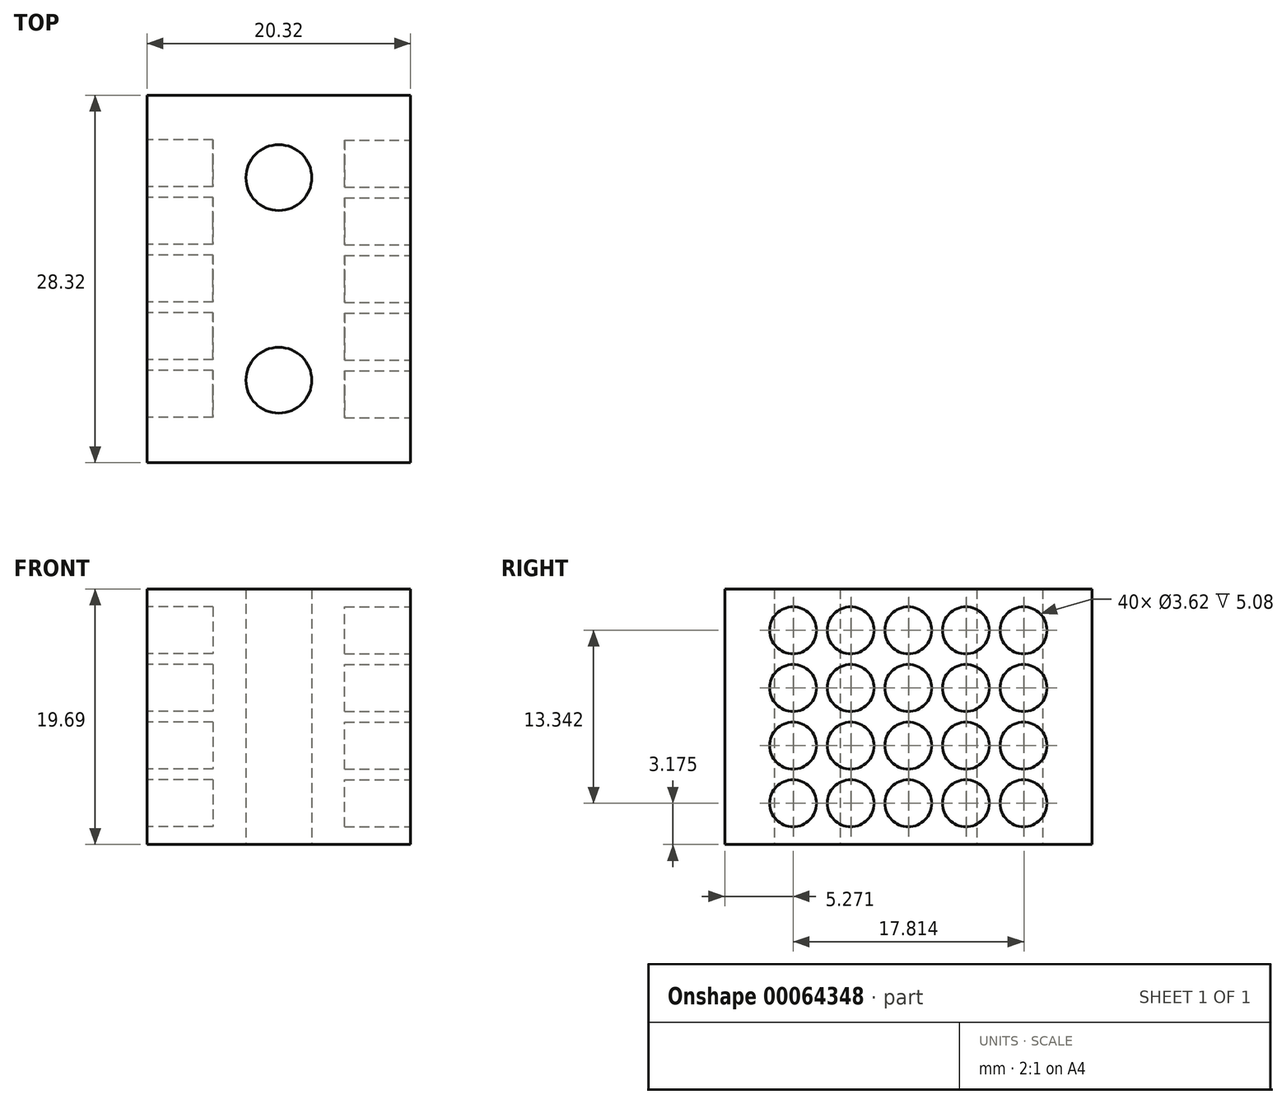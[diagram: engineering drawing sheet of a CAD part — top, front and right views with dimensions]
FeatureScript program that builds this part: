
annotation { "Feature Type Name" : "Feature", "Feature Type Description" : "" }
export const myFeature = defineFeature(function(context is Context, id is Id, definition is map)
    precondition{}
    {
        {
            var Q0;
            Q0=qCreatedBy(makeId("Top.planeOp"),FACE);
            var sketch = newSketch(context, id + "F0", { "sketchPlane" : qUnion([Q0])});
            skLineSegment(sketch, "E0.bottom", {"start": v(0, 0) * mm, "end": v(-20.32, 0) * mm});
            skLineSegment(sketch, "E0.top", {"start": v(0, 28.32) * mm, "end": v(-20.32, 28.32) * mm});
            skLineSegment(sketch, "E0.left", {"start": v(0, 0) * mm, "end": v(0, 28.32) * mm});
            skLineSegment(sketch, "E0.right", {"start": v(-20.32, 0) * mm, "end": v(-20.32, 28.32) * mm});
            skCircle(sketch, "E1", {"center": v(-10.16, 21.97) * mm, "radius": 2.54 * mm});
            skCircle(sketch, "E2", {"center": v(-10.16, 6.35) * mm, "radius": 2.54 * mm});
            skLineSegment(sketch, "E3", {"start": v(-10.16, 21.97) * mm, "end": v(-20.32, 21.97) * mm, "construction": true});
            skLineSegment(sketch, "E4", {"start": v(-10.16, 21.97) * mm, "end": v(0, 21.97) * mm, "construction": true});
            skSolve(sketch);
        }
        {
            var Q0;
            Q0=qSketchRegion(id+"F0",true);
            extrude(context, id + "F1", {"entities" : qUnion([Q0]), "depth" : 19.68 * mm});
        }
        {
            var Q0;
            Q0=makeQuery(id+"F1.opExtrude","SWEPT_FACE",FACE,{"disambiguationData":[OSD([sQuery(id+"F0.wireOp",EDGE,"E0.left")])]});
            var sketch = newSketch(context, id + "F2", { "sketchPlane" : qUnion([Q0])});
            skCircle(sketch, "E5", {"center": v(5.27, 16.51) * mm, "radius": 1.8 * mm});
            skCircle(sketch, "E6.1.0.0", {"center": v(9.72, 16.5) * mm, "radius": 1.8 * mm});
            skCircle(sketch, "E6.2.0.0", {"center": v(14.16, 16.51) * mm, "radius": 1.8 * mm});
            skCircle(sketch, "E6.3.0.0", {"center": v(18.6, 16.51) * mm, "radius": 1.8 * mm});
            skLineSegment(sketch, "E6.direction1", {"start": v(5.27, 16.51) * mm, "end": v(9.72, 16.51) * mm, "construction": true});
            skCircle(sketch, "E7.0.4.0", {"center": v(23.05, 16.51) * mm, "radius": 1.8 * mm});
            skCircle(sketch, "E8.1.0.0", {"center": v(23.05, 12.06) * mm, "radius": 1.8 * mm});
            skLineSegment(sketch, "E8.1.0.1", {"start": v(5.27, 12.06) * mm, "end": v(9.72, 12.06) * mm, "construction": true});
            skCircle(sketch, "E8.1.0.2", {"center": v(18.6, 12.06) * mm, "radius": 1.8 * mm});
            skCircle(sketch, "E8.1.0.3", {"center": v(14.16, 12.06) * mm, "radius": 1.8 * mm});
            skCircle(sketch, "E8.1.0.4", {"center": v(9.72, 12.06) * mm, "radius": 1.8 * mm});
            skCircle(sketch, "E8.1.0.5", {"center": v(5.27, 12.06) * mm, "radius": 1.8 * mm});
            skCircle(sketch, "E8.2.0.0", {"center": v(23.05, 7.62) * mm, "radius": 1.8 * mm});
            skLineSegment(sketch, "E8.2.0.1", {"start": v(5.27, 7.62) * mm, "end": v(9.72, 7.62) * mm, "construction": true});
            skCircle(sketch, "E8.2.0.2", {"center": v(18.6, 7.62) * mm, "radius": 1.8 * mm});
            skCircle(sketch, "E8.2.0.3", {"center": v(14.16, 7.62) * mm, "radius": 1.8 * mm});
            skCircle(sketch, "E8.2.0.4", {"center": v(9.72, 7.62) * mm, "radius": 1.8 * mm});
            skCircle(sketch, "E8.2.0.5", {"center": v(5.27, 7.62) * mm, "radius": 1.8 * mm});
            skCircle(sketch, "E8.3.0.0", {"center": v(23.05, 3.17) * mm, "radius": 1.8 * mm});
            skLineSegment(sketch, "E8.3.0.1", {"start": v(5.27, 3.17) * mm, "end": v(9.72, 3.17) * mm, "construction": true});
            skCircle(sketch, "E8.3.0.2", {"center": v(18.6, 3.17) * mm, "radius": 1.8 * mm});
            skCircle(sketch, "E8.3.0.3", {"center": v(14.16, 3.17) * mm, "radius": 1.8 * mm});
            skCircle(sketch, "E8.3.0.4", {"center": v(9.72, 3.17) * mm, "radius": 1.8 * mm});
            skCircle(sketch, "E8.3.0.5", {"center": v(5.27, 3.17) * mm, "radius": 1.8 * mm});
            skLineSegment(sketch, "E8.direction1", {"start": v(23.05, 16.51) * mm, "end": v(23.05, 12.06) * mm, "construction": true});
            skPoint(sketch, "E9", {"position": v(0, 19.69) * mm});
            skSolve(sketch);
        }
        {
            var Q0;
            Q0=qSketchRegion(id+"F2",true);
            extrude(context, id + "F3", {"entities" : qUnion([Q0]), "operationType" : NewBodyOperationType.REMOVE, "oppositeDirection" : true, "depth" : 5.08 * mm});
        }
        {
            var Q0;
            Q0=makeQuery(id+"F1.opExtrude","SWEPT_FACE",FACE,{"disambiguationData":[OSD([sQuery(id+"F0.wireOp",EDGE,"E0.right")])]});
            var sketch = newSketch(context, id + "F4", { "sketchPlane" : qUnion([Q0])});
            skCircle(sketch, "E10", {"center": v(-23.08, 16.52) * mm, "radius": 1.8 * mm});
            skCircle(sketch, "E11.1.0.0", {"center": v(-18.64, 16.52) * mm, "radius": 1.8 * mm});
            skCircle(sketch, "E11.2.0.0", {"center": v(-14.2, 16.52) * mm, "radius": 1.8 * mm});
            skCircle(sketch, "E11.3.0.0", {"center": v(-9.75, 16.52) * mm, "radius": 1.8 * mm});
            skLineSegment(sketch, "E11.direction1", {"start": v(-23.08, 16.52) * mm, "end": v(-18.64, 16.52) * mm, "construction": true});
            skCircle(sketch, "E12.0.4.0", {"center": v(-5.3, 16.52) * mm, "radius": 1.8 * mm});
            skCircle(sketch, "E13.1.0.0", {"center": v(-5.3, 12.07) * mm, "radius": 1.8 * mm});
            skLineSegment(sketch, "E13.1.0.1", {"start": v(-23.08, 12.07) * mm, "end": v(-18.64, 12.07) * mm, "construction": true});
            skCircle(sketch, "E13.1.0.2", {"center": v(-9.75, 12.07) * mm, "radius": 1.8 * mm});
            skCircle(sketch, "E13.1.0.3", {"center": v(-14.2, 12.07) * mm, "radius": 1.8 * mm});
            skCircle(sketch, "E13.1.0.4", {"center": v(-18.64, 12.07) * mm, "radius": 1.8 * mm});
            skCircle(sketch, "E13.1.0.5", {"center": v(-23.08, 12.07) * mm, "radius": 1.8 * mm});
            skCircle(sketch, "E13.2.0.0", {"center": v(-5.3, 7.63) * mm, "radius": 1.8 * mm});
            skLineSegment(sketch, "E13.2.0.1", {"start": v(-23.08, 7.63) * mm, "end": v(-18.64, 7.63) * mm, "construction": true});
            skCircle(sketch, "E13.2.0.2", {"center": v(-9.75, 7.63) * mm, "radius": 1.8 * mm});
            skCircle(sketch, "E13.2.0.3", {"center": v(-14.2, 7.63) * mm, "radius": 1.8 * mm});
            skCircle(sketch, "E13.2.0.4", {"center": v(-18.64, 7.63) * mm, "radius": 1.8 * mm});
            skCircle(sketch, "E13.2.0.5", {"center": v(-23.08, 7.63) * mm, "radius": 1.8 * mm});
            skCircle(sketch, "E13.3.0.0", {"center": v(-5.3, 3.18) * mm, "radius": 1.8 * mm});
            skLineSegment(sketch, "E13.3.0.1", {"start": v(-23.08, 3.18) * mm, "end": v(-18.64, 3.18) * mm, "construction": true});
            skCircle(sketch, "E13.3.0.2", {"center": v(-9.75, 3.18) * mm, "radius": 1.8 * mm});
            skCircle(sketch, "E13.3.0.3", {"center": v(-14.2, 3.18) * mm, "radius": 1.8 * mm});
            skCircle(sketch, "E13.3.0.4", {"center": v(-18.64, 3.18) * mm, "radius": 1.8 * mm});
            skCircle(sketch, "E13.3.0.5", {"center": v(-23.08, 3.18) * mm, "radius": 1.8 * mm});
            skLineSegment(sketch, "E13.direction1", {"start": v(-5.3, 16.52) * mm, "end": v(-5.3, 12.07) * mm, "construction": true});
            skPoint(sketch, "E14", {"position": v(-28.36, 19.7) * mm});
            skSolve(sketch);
        }
        {
            var Q0;
            Q0 = qSketchRegion(id + "F4", true);
            extrude(context, id + "F5", {"entities" : qUnion([Q0]), "operationType" : NewBodyOperationType.REMOVE, "oppositeDirection" : true, "depth" : 5.08 * mm});
        }
    });
